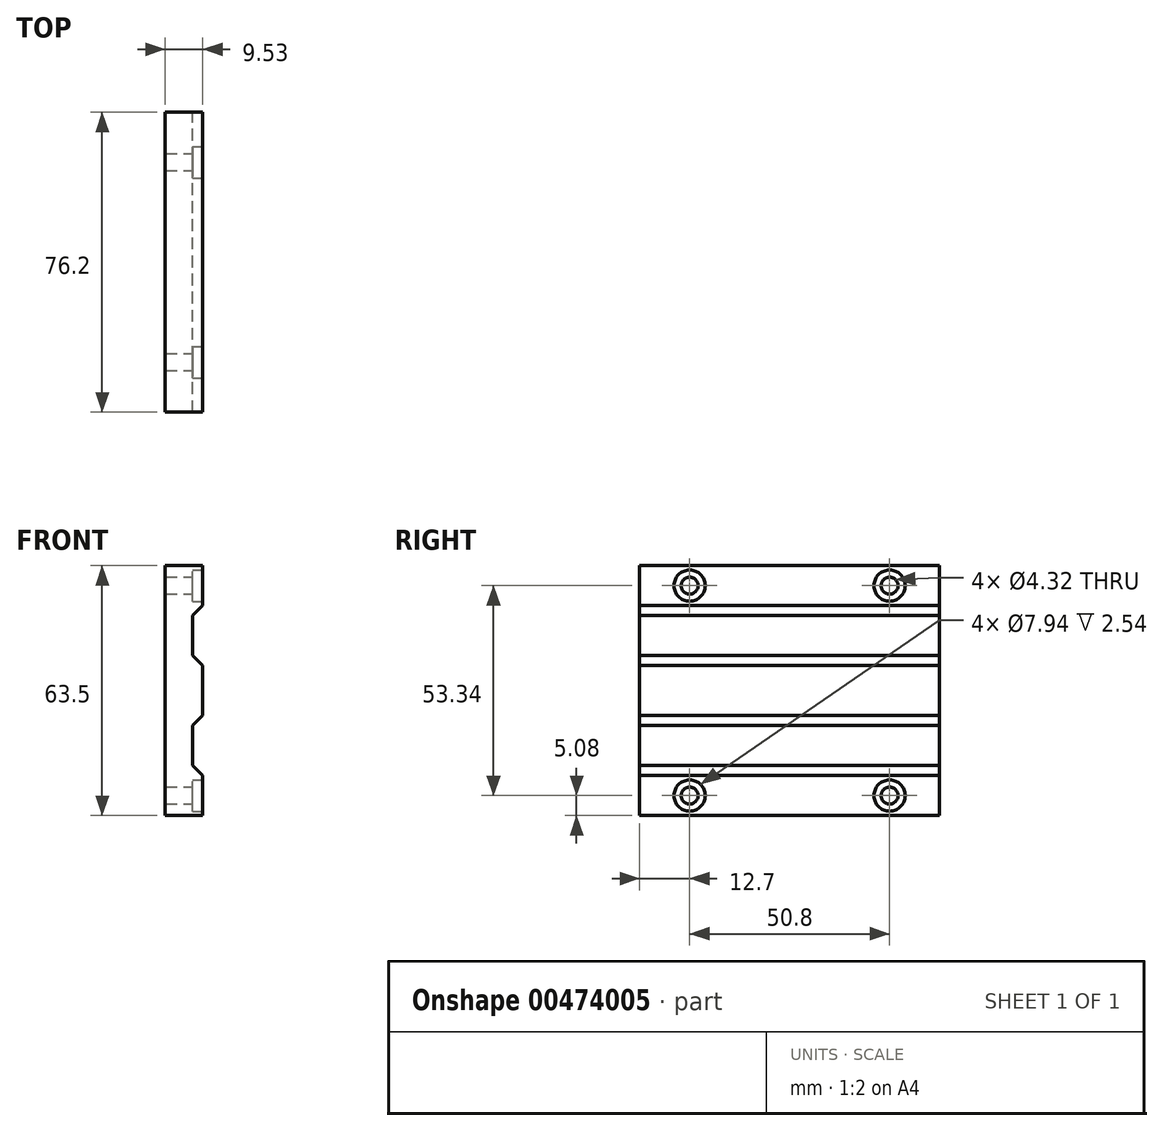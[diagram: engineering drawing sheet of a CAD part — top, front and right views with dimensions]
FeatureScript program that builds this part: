
annotation { "Feature Type Name" : "Feature", "Feature Type Description" : "" }
export const myFeature = defineFeature(function(context is Context, id is Id, definition is map)
    precondition{}
    {
        {
            var Q0;
            Q0=qCreatedBy(makeId("Front.planeOp"),FACE);
            var sketch = newSketch(context, id + "F0", { "sketchPlane" : qUnion([Q0])});
            skLineSegment(sketch, "E0.bottom", {"start": v(0, 0) * mm, "end": v(9.53, 0) * mm});
            skLineSegment(sketch, "E0.top", {"start": v(0, 63.5) * mm, "end": v(9.52, 63.5) * mm});
            skLineSegment(sketch, "E0.left", {"start": v(0, 0) * mm, "end": v(0, 63.5) * mm});
            skLineSegment(sketch, "E0.right", {"start": v(9.53, 0) * mm, "end": v(9.52, 63.5) * mm});
            skPoint(sketch, "E1.endSnap0", {"position": v(4.76, 63.5) * mm});
            skLineSegment(sketch, "E2", {"start": v(6.98, 50.8) * mm, "end": v(6.98, 40.64) * mm});
            skLineSegment(sketch, "E3", {"start": v(6.98, 40.64) * mm, "end": v(9.52, 38.1) * mm});
            skLineSegment(sketch, "E4", {"start": v(9.53, 25.4) * mm, "end": v(6.98, 22.86) * mm});
            skLineSegment(sketch, "E5", {"start": v(6.98, 22.86) * mm, "end": v(6.99, 12.7) * mm});
            skLineSegment(sketch, "E6", {"start": v(6.99, 12.7) * mm, "end": v(9.53, 10.16) * mm});
            skLineSegment(sketch, "E7", {"start": v(6.98, 50.8) * mm, "end": v(9.52, 53.34) * mm});
            skSolve(sketch);
        }
        {
            var Q0;
            {var subQ5=sQuery(id+"F0.wireOp",EDGE,"E0.bottom");Q0=makeQuery(id+"F0.imprint","IMPRINT",FACE,{"disambiguationData":[TD([[makeQuery(id+"F0.imprint","IMPRINT",EDGE,{"derivedFrom":subQ5}),1.0]])]});}
            extrude(context, id + "F1", {"entities" : qUnion([Q0]), "depth" : 76.2 * mm});
        }
        {
            var Q0;
            Q0=makeQuery(id+"F1.opExtrude","CAP_FACE",FACE,{"disambiguationData":[OSD([sQuery(id+"F0.wireOp",EDGE,"E0.bottom"),sQuery(id+"F0.wireOp",EDGE,"E0.top"),sQuery(id+"F0.wireOp",EDGE,"E0.left"),sQuery(id+"F0.wireOp",EDGE,"E0.right"),sQuery(id+"F0.wireOp",EDGE,"E2"),sQuery(id+"F0.wireOp",EDGE,"E3"),sQuery(id+"F0.wireOp",EDGE,"E4"),sQuery(id+"F0.wireOp",EDGE,"E5"),sQuery(id+"F0.wireOp",EDGE,"E6"),sQuery(id+"F0.wireOp",EDGE,"E7")])],"isStart":false});
            var sketch = newSketch(context, id + "F2", { "sketchPlane" : qUnion([Q0])});
            skLineSegment(sketch, "E8.0.0", {"start": v(6.98, 40.64) * mm, "end": v(6.98, 50.8) * mm});
            skLineSegment(sketch, "E8.0.1", {"start": v(6.98, 50.8) * mm, "end": v(9.52, 53.34) * mm});
            skLineSegment(sketch, "E8.0.2", {"start": v(9.52, 53.34) * mm, "end": v(9.52, 63.5) * mm});
            skLineSegment(sketch, "E8.0.3", {"start": v(9.52, 63.5) * mm, "end": v(0, 63.5) * mm});
            skLineSegment(sketch, "E8.0.4", {"start": v(0, 63.5) * mm, "end": v(0, 0) * mm});
            skLineSegment(sketch, "E8.0.5", {"start": v(0, 0) * mm, "end": v(9.53, 0) * mm});
            skLineSegment(sketch, "E8.0.6", {"start": v(9.53, 0) * mm, "end": v(9.53, 10.16) * mm});
            skLineSegment(sketch, "E8.0.7", {"start": v(9.53, 10.16) * mm, "end": v(6.99, 12.7) * mm});
            skLineSegment(sketch, "E8.0.8", {"start": v(6.99, 12.7) * mm, "end": v(6.98, 22.86) * mm});
            skLineSegment(sketch, "E8.0.9", {"start": v(6.98, 22.86) * mm, "end": v(9.53, 25.4) * mm});
            skLineSegment(sketch, "E8.0.10", {"start": v(9.53, 25.4) * mm, "end": v(9.52, 38.1) * mm});
            skLineSegment(sketch, "E8.0.11", {"start": v(9.52, 38.1) * mm, "end": v(6.98, 40.64) * mm});
            skSolve(sketch);
        }
        {
            var Q0;
            {var subQ0=sQuery(id+"F0.wireOp",EDGE,"E0.right");Q0=makeQuery(id+"F1.opExtrude","SWEPT_FACE",FACE,{"disambiguationData":[OSD([subQ0]),TDD([makeQuery(id+"F0.imprint","IMPRINT",EDGE,{"disambiguationData":[TD([[makeQuery(id+"F0.imprint","INTERSECT",VERTEX,{"derivedFrom":[sQuery(id+"F0.wireOp",EDGE,"E0.top"),subQ0]}),1.0]])],"derivedFrom":subQ0})])]});}
            var sketch = newSketch(context, id + "F3", { "sketchPlane" : qUnion([Q0])});
            skPoint(sketch, "E9", {"position": v(-63.5, 58.42) * mm});
            skPoint(sketch, "E9.positionSnap0", {"position": v(-76.2, 58.42) * mm});
            skPoint(sketch, "E10", {"position": v(-12.7, 58.42) * mm});
            skPoint(sketch, "E11", {"position": v(-12.7, 5.08) * mm});
            skPoint(sketch, "E12", {"position": v(-63.5, 5.08) * mm});
            skSolve(sketch);
        }
        {
            var Q0;
            Q0=sQuery(id+"F3.wireOp",VERTEX,"E9");
            var Q1;
            Q1=sQuery(id+"F3.wireOp",VERTEX,"E10");
            var Q2;
            Q2=sQuery(id+"F3.wireOp",VERTEX,"E12");
            var Q3;
            Q3=sQuery(id+"F3.wireOp",VERTEX,"E11");
            var Q4;
            Q4=makeQuery(id+"F1.opExtrude","SWEPT_BODY",BODY,{"disambiguationData":[OSD([sQuery(id+"F0.wireOp",EDGE,"E0.bottom"),sQuery(id+"F0.wireOp",EDGE,"E0.top"),sQuery(id+"F0.wireOp",EDGE,"E0.left"),sQuery(id+"F0.wireOp",EDGE,"E0.right"),sQuery(id+"F0.wireOp",EDGE,"E2"),sQuery(id+"F0.wireOp",EDGE,"E3"),sQuery(id+"F0.wireOp",EDGE,"E4"),sQuery(id+"F0.wireOp",EDGE,"E5"),sQuery(id+"F0.wireOp",EDGE,"E6"),sQuery(id+"F0.wireOp",EDGE,"E7")])]});
            hole(context, id + "F4", {"style" : HoleStyle.SIMPLE, "endStyle" : HoleEndStyle.BLIND, "standardTappedOrClearance" : lookupTablePath({ "standard" : "ANSI", "fit" : "Close", "size" : "#8", "type" : "Clearance" }), "standardBlindInLast" : lookupTablePath({ "fit" : "Close", "standard" : "ANSI", "size" : "#8", "type" : "Clearance" }), "holeDiameter" : 4.32 * mm, "holeDepth" : 12.7 * mm, "isTappedThrough" : true, "tappedDepth" : 10.32 * mm, "tapClearance" : 3, "locations" : qUnion([Q0, Q1, Q2, Q3]), "scope" : qUnion([Q4])});
        }
        {
            var Q0;
            {var subQ0=sQuery(id+"F0.wireOp",EDGE,"E0.right");Q0=makeQuery(id+"F1.opExtrude","SWEPT_FACE",FACE,{"disambiguationData":[OSD([subQ0]),TDD([makeQuery(id+"F0.imprint","IMPRINT",EDGE,{"disambiguationData":[TD([[makeQuery(id+"F0.imprint","INTERSECT",VERTEX,{"derivedFrom":[sQuery(id+"F0.wireOp",EDGE,"E0.top"),subQ0]}),1.0]])],"derivedFrom":subQ0})])]});}
            var sketch = newSketch(context, id + "F5", { "sketchPlane" : qUnion([Q0])});
            skCircle(sketch, "E13", {"center": v(-63.5, 58.42) * mm, "radius": 3.97 * mm});
            skCircle(sketch, "E14", {"center": v(-12.7, 58.42) * mm, "radius": 3.97 * mm});
            skLineSegment(sketch, "E15.0.0", {"start": v(0, 0) * mm, "end": v(0, 10.16) * mm});
            skLineSegment(sketch, "E15.0.1", {"start": v(0, 10.16) * mm, "end": v(-76.2, 10.16) * mm});
            skLineSegment(sketch, "E15.0.2", {"start": v(-76.2, 10.16) * mm, "end": v(-76.2, 0) * mm});
            skLineSegment(sketch, "E15.0.3", {"start": v(-76.2, 0) * mm, "end": v(0, 0) * mm});
            skCircle(sketch, "E16.0", {"center": v(-63.5, 5.08) * mm, "radius": 2.16 * mm});
            skCircle(sketch, "E17.0", {"center": v(-12.7, 5.08) * mm, "radius": 2.16 * mm});
            skCircle(sketch, "E18", {"center": v(-63.5, 5.08) * mm, "radius": 3.97 * mm});
            skCircle(sketch, "E19", {"center": v(-12.7, 5.08) * mm, "radius": 3.97 * mm});
            skSolve(sketch);
        }
        {
            var Q0;
            Q0=makeQuery(id+"F5.imprint","IMPRINT",FACE,{"disambiguationData":[TD([[makeQuery(id+"F5.imprint","IMPRINT",EDGE,{"derivedFrom":sQuery(id+"F5.wireOp",EDGE,"E13")}),1.0]])]});
            var Q1;
            Q1=makeQuery(id+"F5.imprint","IMPRINT",FACE,{"disambiguationData":[TD([[makeQuery(id+"F5.imprint","IMPRINT",EDGE,{"derivedFrom":sQuery(id+"F5.wireOp",EDGE,"E14")}),1.0]])]});
            var Q2;
            Q2=makeQuery(id+"F5.imprint","IMPRINT",FACE,{"disambiguationData":[TD([[makeQuery(id+"F5.imprint","IMPRINT",EDGE,{"derivedFrom":sQuery(id+"F5.wireOp",EDGE,"E16.0")}),-1.0]])]});
            var Q3;
            Q3=makeQuery(id+"F5.imprint","IMPRINT",FACE,{"disambiguationData":[TD([[makeQuery(id+"F5.imprint","IMPRINT",EDGE,{"derivedFrom":sQuery(id+"F5.wireOp",EDGE,"E17.0")}),-1.0]])]});
            extrude(context, id + "F6", {"entities" : qUnion([Q0, Q1, Q2, Q3]), "operationType" : NewBodyOperationType.REMOVE, "oppositeDirection" : true, "depth" : 2.54 * mm, "offsetDistance" : 25.4 * mm});
        }
    });
